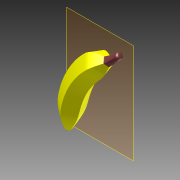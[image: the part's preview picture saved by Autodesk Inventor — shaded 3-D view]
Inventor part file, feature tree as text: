
AUTODESK INVENTOR PART (.ipt)
format: ipt  version: 2014 (Build 180170000, 170)  size: 707,584 bytes
history: native  units: in
note: dims shown in document units (in); Inventor stores cm internally (conversion verified against a paired STEP export)
features: other x2, plane x1, imported_body x1
ambient origin geometry x8: Origin, YZ Plane, XZ Plane, XY Plane, X Axis, Y Axis, Z Axis, Center Point
bodies: Body1 (feature_tree)
feature tree (4):
  other  "PartBody"
  other  "BANANA.CATPart1"
  plane  "Work Plane1"
  imported_body  "Base1"
